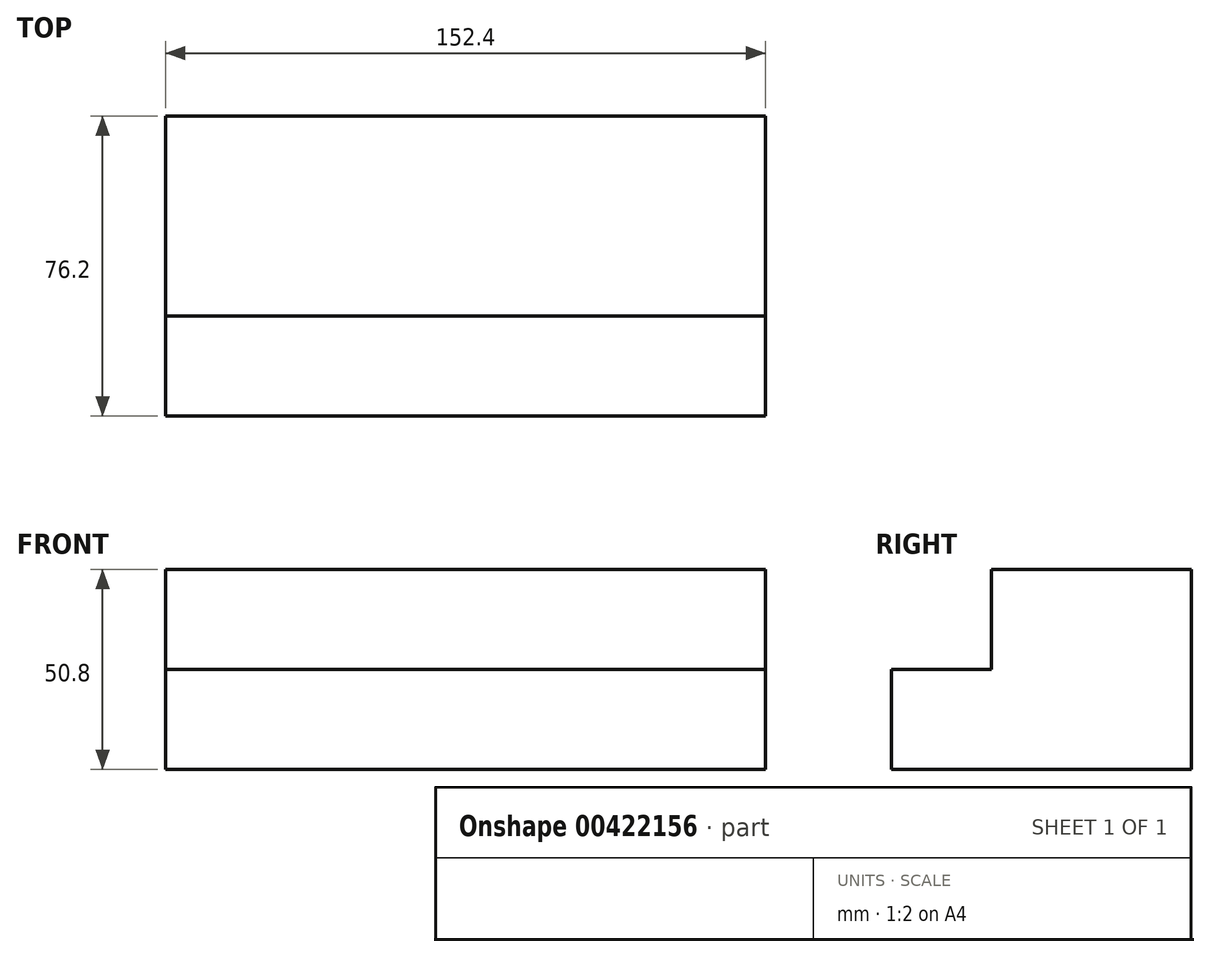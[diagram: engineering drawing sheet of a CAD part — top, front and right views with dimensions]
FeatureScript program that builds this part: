
annotation { "Feature Type Name" : "Feature", "Feature Type Description" : "" }
export const myFeature = defineFeature(function(context is Context, id is Id, definition is map)
    precondition{}
    {
        {
            var Q0;
            Q0=qCreatedBy(makeId("Front.planeOp"),FACE);
            var sketch = newSketch(context, id + "F0", { "sketchPlane" : qUnion([Q0])});
            skLineSegment(sketch, "E0", {"start": v(0, 0) * mm, "end": v(152.4, 0) * mm});
            skLineSegment(sketch, "E1", {"start": v(152.4, 0) * mm, "end": v(152.4, 50.8) * mm});
            skLineSegment(sketch, "E2", {"start": v(152.4, 50.8) * mm, "end": v(0, 50.8) * mm});
            skLineSegment(sketch, "E3", {"start": v(0, 50.8) * mm, "end": v(0, 0) * mm});
            skSolve(sketch);
        }
        {
            var Q0;
            Q0=makeQuery(id+"F0.imprint","IMPRINT",FACE,{"disambiguationData":[TD([[makeQuery(id+"F0.imprint","IMPRINT",EDGE,{"derivedFrom":sQuery(id+"F0.wireOp",EDGE,"E0")}),1.0]])]});
            extrude(context, id + "F1", {"entities" : qUnion([Q0]), "depth" : 76.2 * mm});
        }
        {
            var Q0;
            Q0=makeQuery(id+"F1.opExtrude","CAP_FACE",FACE,{"disambiguationData":[OSD([sQuery(id+"F0.wireOp",EDGE,"E0"),sQuery(id+"F0.wireOp",EDGE,"E1"),sQuery(id+"F0.wireOp",EDGE,"E2"),sQuery(id+"F0.wireOp",EDGE,"E3")])],"isStart":false});
            var sketch = newSketch(context, id + "F2", { "sketchPlane" : qUnion([Q0])});
            skLineSegment(sketch, "E4", {"start": v(0, 0) * mm, "end": v(0, 25.4) * mm});
            skLineSegment(sketch, "E5", {"start": v(0, 25.4) * mm, "end": v(152.4, 25.4) * mm});
            skLineSegment(sketch, "E6", {"start": v(152.4, 25.4) * mm, "end": v(152.4, 0) * mm});
            skLineSegment(sketch, "E7", {"start": v(152.4, 0) * mm, "end": v(0, 0) * mm});
            skSolve(sketch);
        }
        {
            var Q0;
            {var subQ0=sQuery(id+"F2.wireOp",EDGE,"E5");Q0=makeQuery(id+"F2.imprint","IMPRINT",FACE,{"disambiguationData":[TD([[makeQuery(id+"F2.imprint","IMPRINT",EDGE,{"derivedFrom":subQ0}),1.0]])]});}
            extrude(context, id + "F3", {"entities" : qUnion([Q0]), "operationType" : NewBodyOperationType.REMOVE, "oppositeDirection" : true, "depth" : 25.4 * mm});
        }
    });
